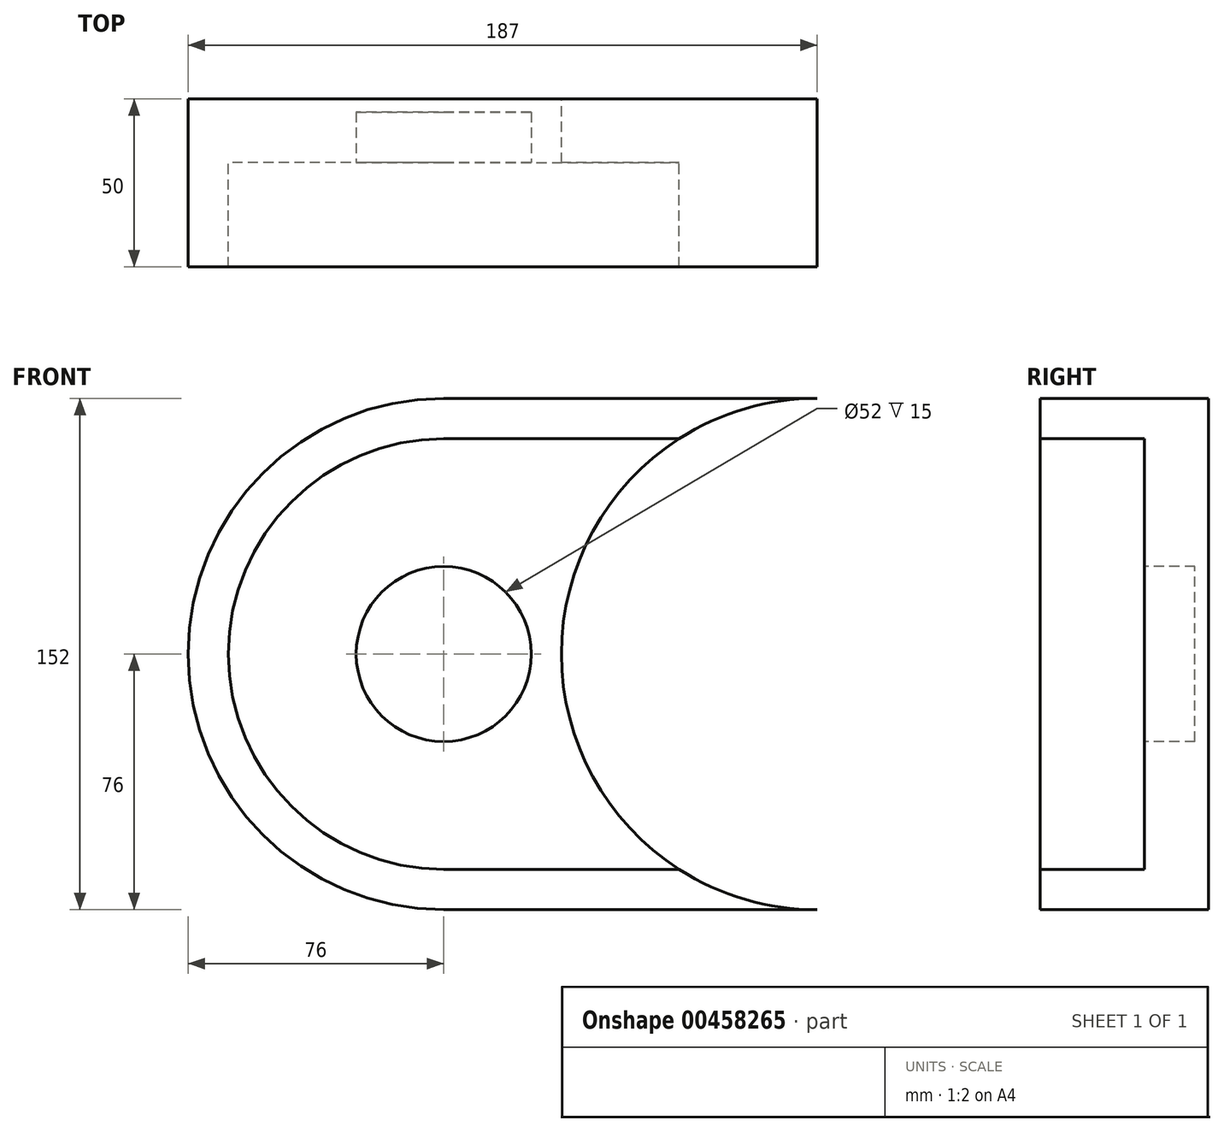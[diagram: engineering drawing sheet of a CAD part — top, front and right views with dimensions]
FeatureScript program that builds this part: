
annotation { "Feature Type Name" : "Feature", "Feature Type Description" : "" }
export const myFeature = defineFeature(function(context is Context, id is Id, definition is map)
    precondition{}
    {
        {
            var Q0;
            Q0=qCreatedBy(makeId("Front.planeOp"),FACE);
            var sketch = newSketch(context, id + "F0", { "sketchPlane" : qUnion([Q0])});
            skCircle(sketch, "E0", {"center": v(0, 0) * mm, "radius": 76 * mm});
            skCircle(sketch, "E1", {"center": v(111, 0) * mm, "radius": 76 * mm});
            skLineSegment(sketch, "E2", {"start": v(0, 76) * mm, "end": v(111, 76) * mm});
            skLineSegment(sketch, "E3", {"start": v(0, -76) * mm, "end": v(111, -76) * mm});
            skSolve(sketch);
        }
        {
            var Q0;
            {var subQ0=sQuery(id+"F0.wireOp",EDGE,"E1");var subQ1=sQuery(id+"F0.wireOp",EDGE,"E0");var subQ2=makeQuery(id+"F0.imprint","INTERSECT",VERTEX,{"disambiguationData":[OD(0.0)],"derivedFrom":[subQ1,subQ0]});Q0=makeQuery(id+"F0.imprint","IMPRINT",FACE,{"disambiguationData":[TD([[makeQuery(id+"F0.imprint","IMPRINT",EDGE,{"disambiguationData":[TD([[subQ2,1.0]])],"derivedFrom":subQ1}),-1.0]])]});}
            var Q1;
            {var subQ0=sQuery(id+"F0.wireOp",EDGE,"E2");Q1=makeQuery(id+"F0.imprint","IMPRINT",FACE,{"disambiguationData":[TD([[makeQuery(id+"F0.imprint","IMPRINT",EDGE,{"derivedFrom":subQ0}),-1.0]])]});}
            var Q2;
            {var subQ0=sQuery(id+"F0.wireOp",EDGE,"E1");var subQ1=sQuery(id+"F0.wireOp",EDGE,"E0");var subQ2=makeQuery(id+"F0.imprint","INTERSECT",VERTEX,{"disambiguationData":[OD(0.0)],"derivedFrom":[subQ1,subQ0]});Q2=makeQuery(id+"F0.imprint","IMPRINT",FACE,{"disambiguationData":[TD([[makeQuery(id+"F0.imprint","IMPRINT",EDGE,{"disambiguationData":[TD([[subQ2,1.0]])],"derivedFrom":subQ1}),1.0]])]});}
            var Q3;
            {var subQ0=sQuery(id+"F0.wireOp",EDGE,"E3");Q3=makeQuery(id+"F0.imprint","IMPRINT",FACE,{"disambiguationData":[TD([[makeQuery(id+"F0.imprint","IMPRINT",EDGE,{"derivedFrom":subQ0}),1.0]])]});}
            var Q4;
            {var subQ0=sQuery(id+"F0.wireOp",EDGE,"E0");var subQ1=makeQuery(id+"F0.imprint","INTERSECT",VERTEX,{"derivedFrom":[subQ0,sQuery(id+"F0.wireOp",EDGE,"E2")]});Q4=makeQuery(id+"F0.imprint","IMPRINT",FACE,{"disambiguationData":[TD([[makeQuery(id+"F0.imprint","IMPRINT",EDGE,{"disambiguationData":[TD([[subQ1,1.0]])],"derivedFrom":subQ0}),1.0]])]});}
            extrude(context, id + "F1", {"entities" : qUnion([Q0, Q1, Q2, Q3, Q4]), "depth" : 50 * mm, "offsetDistance" : 25 * mm});
        }
        {
            var Q0;
            Q0=qCreatedBy(makeId("Front.planeOp"),FACE);
            cPlane(context, id + "F2", {"entities" : qUnion([Q0]), "cplaneType" : CPlaneType.OFFSET, "offset" : 19 * mm, "width" : 150 * mm, "height" : 150 * mm});
        }
        {
            var Q0;
            Q0=qCreatedBy(id+"F2.planeOp",FACE);
            var sketch = newSketch(context, id + "F3", { "sketchPlane" : qUnion([Q0])});
            skArc(sketch, "E4", {"start": v(0, 64) * mm, "mid": v(-64, 0) * mm, "end": v(0, -64) * mm});
            skArc(sketch, "E5", {"start": v(111, -64) * mm, "mid": v(175, 0) * mm, "end": v(111, 64) * mm});
            skLineSegment(sketch, "E6", {"start": v(0, 64) * mm, "end": v(111, 64) * mm});
            skLineSegment(sketch, "E7", {"start": v(0, -64) * mm, "end": v(111, -64) * mm});
            skSolve(sketch);
        }
        {
            var Q0;
            Q0 = qSketchRegion(id + "F3", true);
            extrude(context, id + "F4", {"entities" : qUnion([Q0]), "operationType" : NewBodyOperationType.REMOVE, "depth" : 50 * mm, "offsetDistance" : 25 * mm});
        }
        {
            var Q0;
            Q0=qCreatedBy(id+"F2.planeOp",FACE);
            var sketch = newSketch(context, id + "F5", { "sketchPlane" : qUnion([Q0])});
            skCircle(sketch, "E8", {"center": v(0, 0) * mm, "radius": 26 * mm});
            skSolve(sketch);
        }
        {
            var Q0;
            Q0=makeQuery(id+"F5.imprint","IMPRINT",FACE,{"disambiguationData":[TD([[makeQuery(id+"F5.imprint","IMPRINT",EDGE,{"derivedFrom":sQuery(id+"F5.wireOp",EDGE,"E8")}),1.0]])]});
            extrude(context, id + "F6", {"entities" : qUnion([Q0]), "operationType" : NewBodyOperationType.REMOVE, "oppositeDirection" : true, "depth" : 15 * mm, "offsetDistance" : 25 * mm});
        }
        {
            var Q0;
            Q0=qCreatedBy(makeId("Right.planeOp"),FACE);
            cPlane(context, id + "F7", {"entities" : qUnion([Q0]), "cplaneType" : CPlaneType.OFFSET, "offset" : 111 * mm, "width" : 150 * mm, "height" : 150 * mm});
        }
        {
            var Q0;
            Q0=qCreatedBy(id+"F7.planeOp",FACE);
            var sketch = newSketch(context, id + "F8", { "sketchPlane" : qUnion([Q0])});
            skLineSegment(sketch, "E9", {"start": v(24.66, 0) * mm, "end": v(-59.67, 0) * mm, "construction": true});
            skLineSegment(sketch, "E10", {"start": v(0, 0) * mm, "end": v(0, 11) * mm});
            skLineSegment(sketch, "E11", {"start": v(0, 11) * mm, "end": v(-2, 11) * mm});
            skLineSegment(sketch, "E12", {"start": v(-2, 11) * mm, "end": v(-2, 18.5) * mm});
            skLineSegment(sketch, "E13", {"start": v(-2, 18.5) * mm, "end": v(-7, 18.5) * mm});
            skLineSegment(sketch, "E14", {"start": v(-7, 18.5) * mm, "end": v(-7, 23.5) * mm});
            skLineSegment(sketch, "E15", {"start": v(-7, 23.5) * mm, "end": v(-19, 23.5) * mm});
            skLineSegment(sketch, "E16", {"start": v(-19, 23.5) * mm, "end": v(-19, 0) * mm});
            skLineSegment(sketch, "E17", {"start": v(0, 0) * mm, "end": v(-19, 0) * mm});
            skSolve(sketch);
        }
        {
            var Q0;
            Q0 = qSketchRegion(id + "F8", true);
            var Q1;
            Q1=sQuery(id+"F8.wireOp",EDGE,"E9");
            revolve(context, id + "F9", {"operationType" : NewBodyOperationType.REMOVE, "entities" : qUnion([Q0]), "axis" : qUnion([Q1]), "revolveType" : RevolveType.FULL});
        }
    });
